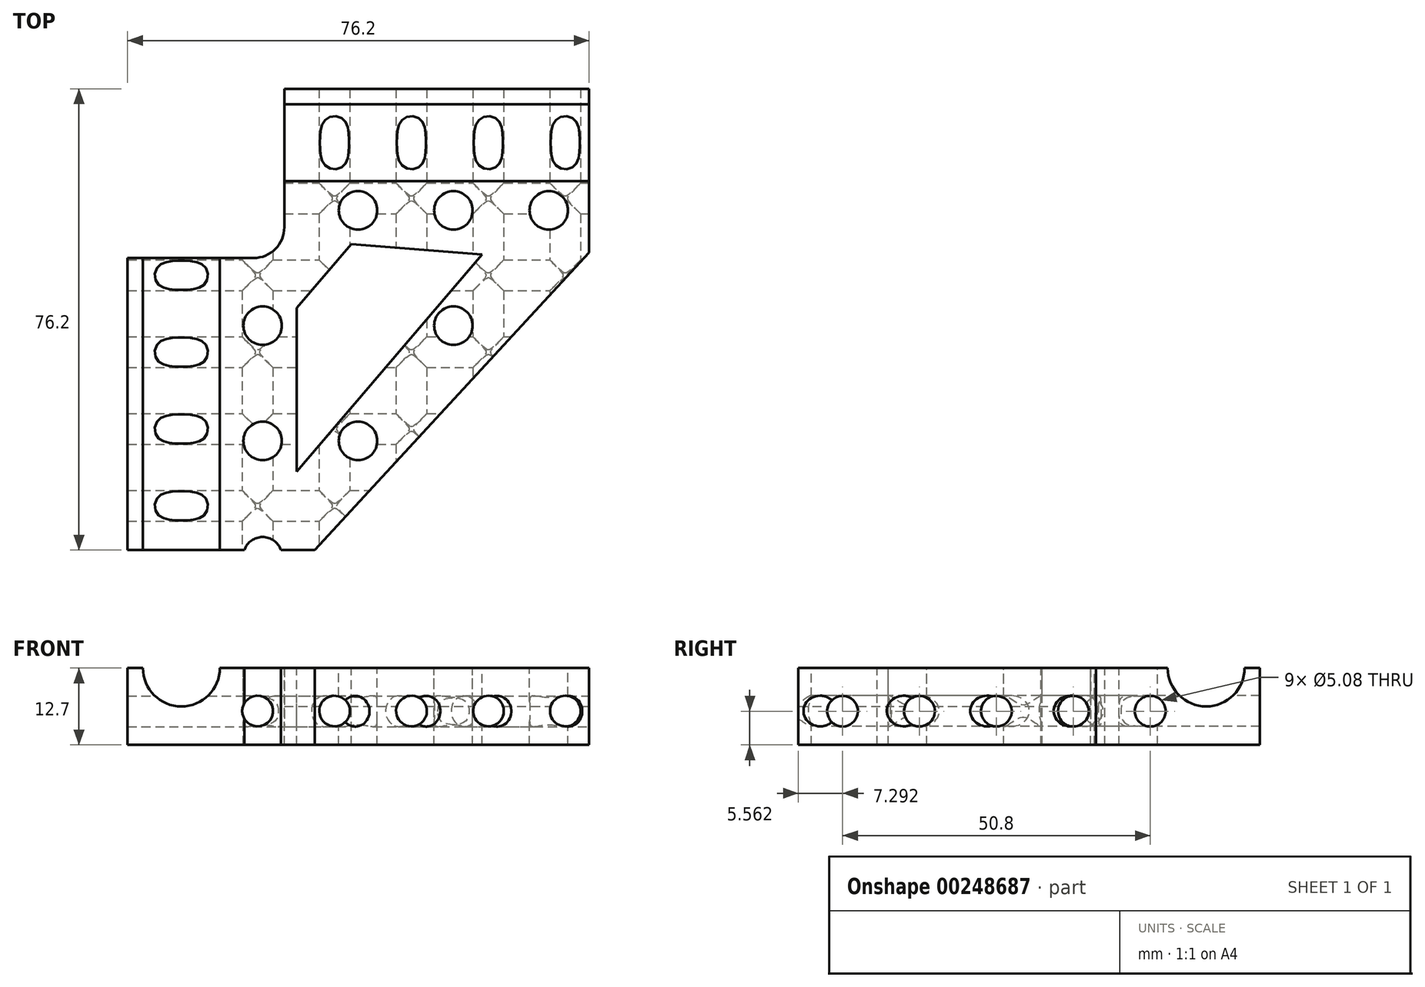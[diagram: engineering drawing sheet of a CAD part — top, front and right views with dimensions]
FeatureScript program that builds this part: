
annotation { "Feature Type Name" : "Feature", "Feature Type Description" : "" }
export const myFeature = defineFeature(function(context is Context, id is Id, definition is map)
    precondition{}
    {
        {
            var Q0;
            Q0=qCreatedBy(makeId("Top.planeOp"),FACE);
            var sketch = newSketch(context, id + "F0", { "sketchPlane" : qUnion([Q0])});
            skLineSegment(sketch, "E0.bottom", {"start": v(0, 0) * mm, "end": v(76.2, 0) * mm});
            skLineSegment(sketch, "E0.top", {"start": v(0, -76.2) * mm, "end": v(76.2, -76.2) * mm});
            skLineSegment(sketch, "E0.left", {"start": v(0, 0) * mm, "end": v(0, -76.2) * mm});
            skLineSegment(sketch, "E0.right", {"start": v(76.2, 0) * mm, "end": v(76.2, -76.2) * mm});
            skSolve(sketch);
        }
        {
            var Q0;
            Q0 = qSketchRegion(id + "F0", true);
            extrude(context, id + "F1", {"entities" : qUnion([Q0]), "depth" : 12.7 * mm});
        }
        {
            var Q0;
            Q0=makeQuery(id+"F1.opExtrude","SWEPT_FACE",FACE,{"disambiguationData":[OSD([sQuery(id+"F0.wireOp",EDGE,"E0.right")])]});
            var sketch = newSketch(context, id + "F2", { "sketchPlane" : qUnion([Q0])});
            skCircle(sketch, "E1", {"center": v(-8.9, 12.7) * mm, "radius": 6.35 * mm});
            skSolve(sketch);
        }
        {
            var Q0;
            Q0 = qSketchRegion(id + "F2", true);
            extrude(context, id + "F3", {"entities" : qUnion([Q0]), "operationType" : NewBodyOperationType.REMOVE, "oppositeDirection" : true, "depth" : 76.2 * mm});
        }
        {
            var Q0;
            Q0=makeQuery(id+"F1.opExtrude","SWEPT_FACE",FACE,{"disambiguationData":[OSD([sQuery(id+"F0.wireOp",EDGE,"E0.bottom")])]});
            var sketch = newSketch(context, id + "F4", { "sketchPlane" : qUnion([Q0])});
            skCircle(sketch, "E2", {"center": v(-8.9, 12.7) * mm, "radius": 6.35 * mm});
            skSolve(sketch);
        }
        {
            var Q0;
            Q0 = qSketchRegion(id + "F4", true);
            extrude(context, id + "F5", {"entities" : qUnion([Q0]), "operationType" : NewBodyOperationType.REMOVE, "oppositeDirection" : true, "depth" : 76.2 * mm});
        }
        {
            var Q0;
            {var subQ0=sQuery(id+"F0.wireOp",EDGE,"E0.top");var subQ1=makeQuery(id+"F1.opExtrude","SWEPT_FACE",FACE,{"disambiguationData":[OSD([subQ0])]});var subQ2=sQuery(id+"F0.wireOp",EDGE,"E0.right");var subQ3=makeQuery(id+"F1.opExtrude","SWEPT_FACE",FACE,{"disambiguationData":[OSD([subQ2])]});var subQ5=sQuery(id+"F0.wireOp",EDGE,"E0.left");Q0=makeQuery(id+"F5.boolean.opBoolean","SPLIT",FACE,{"disambiguationData":[TD([subQ3])],"derivedFrom":makeQuery(id+"F3.boolean.opBoolean","SPLIT",FACE,{"disambiguationData":[TD([subQ1])],"derivedFrom":makeQuery(id+"F1.opExtrude","CAP_FACE",FACE,{"disambiguationData":[OSD([sQuery(id+"F0.wireOp",EDGE,"E0.bottom"),subQ0,subQ5,subQ2])],"isStart":false})})});}
            var sketch = newSketch(context, id + "F6", { "sketchPlane" : qUnion([Q0])});
            skLineSegment(sketch, "E3.bottom", {"start": v(0, 0) * mm, "end": v(25.89, 0) * mm});
            skLineSegment(sketch, "E3.top", {"start": v(0, -27.94) * mm, "end": v(25.89, -27.94) * mm});
            skLineSegment(sketch, "E3.left", {"start": v(0, 0) * mm, "end": v(0, -27.94) * mm});
            skLineSegment(sketch, "E3.right", {"start": v(25.89, 0) * mm, "end": v(25.89, -27.94) * mm});
            skLineSegment(sketch, "E4", {"start": v(76.2, -27.06) * mm, "end": v(30.89, -76.2) * mm});
            skLineSegment(sketch, "E5", {"start": v(30.89, -76.2) * mm, "end": v(76.2, -76.2) * mm});
            skLineSegment(sketch, "E6", {"start": v(76.2, -76.2) * mm, "end": v(76.2, -27.06) * mm});
            skLineSegment(sketch, "E7", {"start": v(27.94, -63.24) * mm, "end": v(58.54, -27.36) * mm});
            skLineSegment(sketch, "E8", {"start": v(27.94, -63.24) * mm, "end": v(27.94, -36.18) * mm});
            skLineSegment(sketch, "E9", {"start": v(27.94, -36.18) * mm, "end": v(36.92, -25.65) * mm});
            skLineSegment(sketch, "E10", {"start": v(36.92, -25.65) * mm, "end": v(58.54, -27.36) * mm});
            skSolve(sketch);
        }
        {
            var Q0;
            Q0=makeQuery(id+"F6.imprint","IMPRINT",FACE,{"disambiguationData":[TD([[makeQuery(id+"F6.imprint","IMPRINT",EDGE,{"derivedFrom":sQuery(id+"F6.wireOp",EDGE,"E4")}),1.0]])]});
            var Q1;
            {var subQ2=sQuery(id+"F6.wireOp",EDGE,"E3.bottom");Q1=makeQuery(id+"F6.imprint","IMPRINT",FACE,{"disambiguationData":[TD([[makeQuery(id+"F6.imprint","IMPRINT",EDGE,{"derivedFrom":subQ2}),-1.0]])]});}
            var Q2;
            {var subQ0=sQuery(id+"F6.wireOp",EDGE,"E3.right");var subQ1=sQuery(id+"F6.wireOp",EDGE,"E3.top");var subQ2=makeQuery(id+"F6.imprint","INTERSECT",VERTEX,{"derivedFrom":[subQ1,subQ0,sQuery(id+"F6.wireOp",EDGE,"SmRdSoHZ-RDkh-LDp3-4icb-4JMMmW0VeU5R"),sQuery(id+"F6.wireOp",EDGE,"gYyAjabg-9KVz-7Cc8-wDzs-BdaCB4d5ci5R")]});Q2=makeQuery(id+"F6.imprint","IMPRINT",FACE,{"disambiguationData":[TD([[makeQuery(id+"F6.imprint","IMPRINT",EDGE,{"disambiguationData":[TD([[subQ2,1.0]])],"derivedFrom":subQ1}),1.0]])]});}
            var Q3;
            Q3=makeQuery(id+"F6.imprint","IMPRINT",FACE,{"disambiguationData":[TD([[makeQuery(id+"F6.imprint","IMPRINT",EDGE,{"derivedFrom":sQuery(id+"F6.wireOp",EDGE,"E7")}),1.0]])]});
            extrude(context, id + "F7", {"entities" : qUnion([Q0, Q1, Q2, Q3]), "operationType" : NewBodyOperationType.REMOVE, "oppositeDirection" : true, "depth" : 25.4 * mm});
        }
        {
            var Q0;
            Q0=makeQuery(id+"F7.boolean.opBoolean","COPY",EDGE,{"derivedFrom":makeQuery(id+"F7.opExtrude","SWEPT_EDGE",EDGE,{"disambiguationData":[OSD([sQuery(id+"F6.wireOp",EDGE,"E3.top"),sQuery(id+"F6.wireOp",EDGE,"E3.right")])]})});
            fillet(context, id + "F8", {"entities" : qUnion([Q0]), "radius" : 5.08 * mm, "tangentPropagation" : true, "allowEdgeOverflow" : false});
        }
        {
            var Q0;
            Q0=makeQuery(id+"F1.opExtrude","SWEPT_FACE",FACE,{"disambiguationData":[OSD([sQuery(id+"F0.wireOp",EDGE,"E0.right")])]});
            var sketch = newSketch(context, id + "F9", { "sketchPlane" : qUnion([Q0])});
            skCircle(sketch, "E11", {"center": v(-18.1, 5.56) * mm, "radius": 2.54 * mm});
            skCircle(sketch, "E12.1.0.0", {"center": v(-30.8, 5.56) * mm, "radius": 2.54 * mm});
            skCircle(sketch, "E12.2.0.0", {"center": v(-43.5, 5.56) * mm, "radius": 2.54 * mm});
            skLineSegment(sketch, "E12.direction1", {"start": v(-18.1, 5.56) * mm, "end": v(-30.8, 5.56) * mm, "construction": true});
            skCircle(sketch, "E13.0.3.0", {"center": v(-56.2, 5.56) * mm, "radius": 2.54 * mm});
            skCircle(sketch, "E13.0.4.0", {"center": v(-68.9, 5.56) * mm, "radius": 2.54 * mm});
            skSolve(sketch);
        }
        {
            var Q0;
            Q0 = qSketchRegion(id + "F9", true);
            extrude(context, id + "F10", {"entities" : qUnion([Q0]), "operationType" : NewBodyOperationType.REMOVE, "oppositeDirection" : true, "depth" : 76.2 * mm});
        }
        {
            var Q0;
            Q0=makeQuery(id+"F1.opExtrude","SWEPT_FACE",FACE,{"disambiguationData":[OSD([sQuery(id+"F0.wireOp",EDGE,"E0.top")])]});
            var sketch = newSketch(context, id + "F11", { "sketchPlane" : qUnion([Q0])});
            skCircle(sketch, "E14", {"center": v(21.47, 5.59) * mm, "radius": 2.54 * mm});
            skCircle(sketch, "E15.1.0.0", {"center": v(34.17, 5.59) * mm, "radius": 2.54 * mm});
            skCircle(sketch, "E15.2.0.0", {"center": v(46.87, 5.59) * mm, "radius": 2.54 * mm});
            skCircle(sketch, "E15.3.0.0", {"center": v(59.57, 5.59) * mm, "radius": 2.54 * mm});
            skCircle(sketch, "E15.4.0.0", {"center": v(72.27, 5.59) * mm, "radius": 2.54 * mm});
            skLineSegment(sketch, "E15.direction1", {"start": v(21.47, 5.59) * mm, "end": v(34.17, 5.59) * mm, "construction": true});
            skSolve(sketch);
        }
        {
            var Q0;
            Q0 = qSketchRegion(id + "F11", true);
            extrude(context, id + "F12", {"entities" : qUnion([Q0]), "operationType" : NewBodyOperationType.REMOVE, "oppositeDirection" : true, "depth" : 76.2 * mm});
        }
        {
            var Q0;
            {var subQ0=sQuery(id+"F0.wireOp",EDGE,"E0.top");var subQ1=makeQuery(id+"F1.opExtrude","SWEPT_FACE",FACE,{"disambiguationData":[OSD([subQ0])]});var subQ2=sQuery(id+"F0.wireOp",EDGE,"E0.right");var subQ3=makeQuery(id+"F1.opExtrude","SWEPT_FACE",FACE,{"disambiguationData":[OSD([subQ2])]});var subQ5=sQuery(id+"F0.wireOp",EDGE,"E0.left");Q0=makeQuery(id+"F5.boolean.opBoolean","SPLIT",FACE,{"disambiguationData":[TD([subQ3])],"derivedFrom":makeQuery(id+"F3.boolean.opBoolean","SPLIT",FACE,{"disambiguationData":[TD([subQ1])],"derivedFrom":makeQuery(id+"F1.opExtrude","CAP_FACE",FACE,{"disambiguationData":[OSD([sQuery(id+"F0.wireOp",EDGE,"E0.bottom"),subQ0,subQ5,subQ2])],"isStart":false})})});}
            var sketch = newSketch(context, id + "F13", { "sketchPlane" : qUnion([Q0])});
            skCircle(sketch, "E16", {"center": v(69.55, -20.07) * mm, "radius": 3.18 * mm});
            skCircle(sketch, "E17.0.1.0", {"center": v(69.55, -39.12) * mm, "radius": 3.18 * mm});
            skCircle(sketch, "E17.0.2.0", {"center": v(69.55, -58.17) * mm, "radius": 3.18 * mm});
            skCircle(sketch, "E17.0.3.0", {"center": v(69.55, -77.22) * mm, "radius": 3.18 * mm});
            skCircle(sketch, "E17.1.0.0", {"center": v(53.8, -20.07) * mm, "radius": 3.18 * mm});
            skCircle(sketch, "E17.1.1.0", {"center": v(53.8, -39.12) * mm, "radius": 3.18 * mm});
            skCircle(sketch, "E17.1.2.0", {"center": v(53.8, -58.17) * mm, "radius": 3.18 * mm});
            skCircle(sketch, "E17.1.3.0", {"center": v(53.8, -77.22) * mm, "radius": 3.18 * mm});
            skCircle(sketch, "E17.2.0.0", {"center": v(38.05, -20.07) * mm, "radius": 3.18 * mm});
            skCircle(sketch, "E17.2.1.0", {"center": v(38.05, -39.12) * mm, "radius": 3.18 * mm});
            skCircle(sketch, "E17.2.2.0", {"center": v(38.05, -58.17) * mm, "radius": 3.18 * mm});
            skCircle(sketch, "E17.2.3.0", {"center": v(38.05, -77.22) * mm, "radius": 3.18 * mm});
            skCircle(sketch, "E17.3.0.0", {"center": v(22.3, -20.07) * mm, "radius": 3.18 * mm});
            skCircle(sketch, "E17.3.1.0", {"center": v(22.3, -39.12) * mm, "radius": 3.18 * mm});
            skCircle(sketch, "E17.3.2.0", {"center": v(22.3, -58.17) * mm, "radius": 3.18 * mm});
            skCircle(sketch, "E17.3.3.0", {"center": v(22.3, -77.22) * mm, "radius": 3.18 * mm});
            skLineSegment(sketch, "E17.direction1", {"start": v(69.55, -20.07) * mm, "end": v(53.8, -20.07) * mm, "construction": true});
            skLineSegment(sketch, "E17.direction2", {"start": v(69.55, -20.07) * mm, "end": v(69.55, -39.12) * mm, "construction": true});
            skSolve(sketch);
        }
        {
            var Q0;
            Q0 = qSketchRegion(id + "F13", true);
            extrude(context, id + "F14", {"entities" : qUnion([Q0]), "operationType" : NewBodyOperationType.REMOVE, "oppositeDirection" : true, "depth" : 25.4 * mm});
        }
    });
